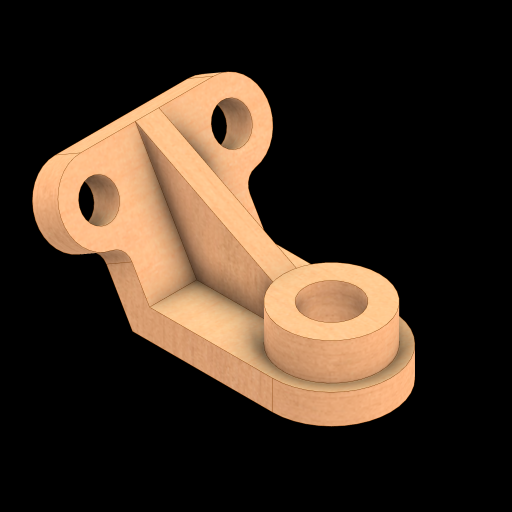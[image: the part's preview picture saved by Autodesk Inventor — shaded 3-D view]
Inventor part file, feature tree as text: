
AUTODESK INVENTOR PART (.ipt)
format: ipt  version: 2024 (Build 280153000, 153)  size: 337,920 bytes
history: native  units: mm
features: extrude x5, sketch x5, fillet x1, hole x1, rib x1, projected_geometry x1
ambient origin geometry x8: Origin, YZ Plane, XZ Plane, XY Plane, X Axis, Y Axis, Z Axis, Center Point
bodies: Solid1 (feature_tree)
feature tree (14):
  extrude  "BASE"  Depth=95.0mm
  extrude  "EARS"  TaperAngle=120.0deg  [1 undecoded]
  fillet  "Fillet1"  Radius=20.0mm
  hole  "EARHOLES"  [1 undecoded]
  sketch  "Sketch4"  dims[d10=45.0mm d11=50.0mm]
  extrude  "ROUNDED END"  Depth=45.0mm
  extrude  "RAISED BOSS"  Depth=10.0mm
  extrude  "BOSS CUTOUT"  Depth=16.0mm
  rib  "Rib1"
  sketch  "Sketch1"  dims[d0=95.0mm d1=95.0mm]
  sketch  "Sketch2"  dims[d2=20.0mm d5=120.0deg d6=20.0mm]
  sketch  "Sketch3"  dims[d7=80.0mm d8=0.0mm d9=90.0mm]
  sketch  "Sketch5"  dims[d12=20.0mm d13=0.0mm d14=10.0mm d15=25.0mm d16=6.0mm d17=4.0mm d18=2.0mm d19=90.0deg d20=8.0mm d21=20.594885mm d22=35.0mm d23=65.0mm d24=20.0mm d25=0.0mm d26=25.0mm d27=0.0mm d28=0.0mm d29=0.0mm d30=1.0mm d31=16.0mm d32=0.0mm d33=0.0mm d34=1.0mm d35=1.0mm]
  projected_geometry  "Projected Loop1"
note: 2 required parameter values undecoded (feature->parameter linkage not recoverable at this tier; creation-order binding heuristic only, values carry confidence <= 0.55)
